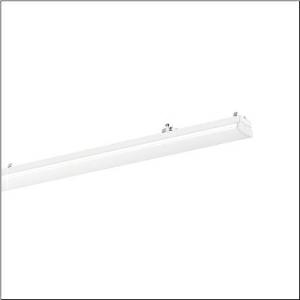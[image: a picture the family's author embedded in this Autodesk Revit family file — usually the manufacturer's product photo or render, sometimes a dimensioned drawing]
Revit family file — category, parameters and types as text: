
# Revit family: licross_r__11_recessed_opal_ho_51tl1dmv4g5m_d39c
name_source: partatom
category: Lighting Fixtures
units: mm (PartAtom-declared; Revit-internal decimal feet)

## family parameters
Cut with Voids When Loaded = No
Host = Face
Light Source = No
Part Type = Normal
Room Calculation Point = No
Round Connector Dimension = Use Diameter
Shared = No

## types (1)
- --- (1 x LED, 16760 lm, 89.2 W, 4000K)
    Apparent Load = 89 VA
    CIE Flux Codes = 44 73 91 87 100
    Color Rendering = 80
    Color Temperature = 4000K
    Default Elevation = 1800 mm
    Description = Licross® 11 recessed opal HO, luminaire insert, of sheet steel, coil coated, white, length: 2.250mm, width: 76mm, height: 87mm, LED rated luminous flux: 16.760lm, light colour: 840, control gear: ON/OFF Multilumen, with plug, 3-pole, with phase selection, mains connection: 220..240V, AC, 50/60Hz, rated input power: 89W, internal wiring halogen-free, primary optical cover: cover, of PMMA, light emission: direct with ceiling illumination distribution, primary light characteristic: symmetric, protection rating (complete): IP40, insulation class (complete): insulation class I (protective earthing), certification: CE, ENEC, VDE, UKCA, protection symbol: D if used in an environment without relevant dust loads with corresponding accessories, impact resistance: IK06, permissible ambient temperature for indoor applications: -35..+35°C, corresponds to IFS (International Featured Standards) requirements for safety and quality in the food industry, reducing of maximum allowable ambient temperature of 5°C with ceiling mounting, packaging unit: 1 piece
    Height = 83 mm
    Lamp = 1 x LED
    Lamp Light Flux = 16760 lm
    Lamp Power = 89.2 W
    Lamp count = 1
    Length = 2250 mm
    Luminous efficacy = 188 lm/W
    Manufacturer = Siteco
    ModVariant = No
    Model = 51TL1DMV4G5M
    Mounting Place = Ceiling
    Mounting Type = Pendant
    Number of Poles = 1
    OnlyDefault = Yes
    Power Factor = 1
    Product Name = Licross® 11 recessed opal HO
    Product group = luminaire insert | ceiling pendant
    ProductGroupID = 902
    Protection Class = Protection class I
    Protection Degree = IP 40
    RLX_Detail_Level = 1
    RLX_Emergency_Light_Flux = 0 lm
    RLX_Emergency_Type = 0
    RLX_Emergency_Type_DB = No
    RlxData = <blob elided: 24501 chars, md5=916fb058>
    Socket = socket
    Standby Power = 0 W
    System Light Flux = 16760 lm
    System Power = 89 W
    Type Comments = factory setting: luminous flux: 100 % | (A | C | E) | 210 mA
    Type Image = l_1313666.jpg
    URL = http://relux.com
    VarID = @adj_097371
    Voltage = 0 V
    Weight = 0.00 kg
    Width = 76 mm

## geometry (parser evidence)
native form markers: Blend x4, Sweep x13
no freeform markers — native parametric forms only
